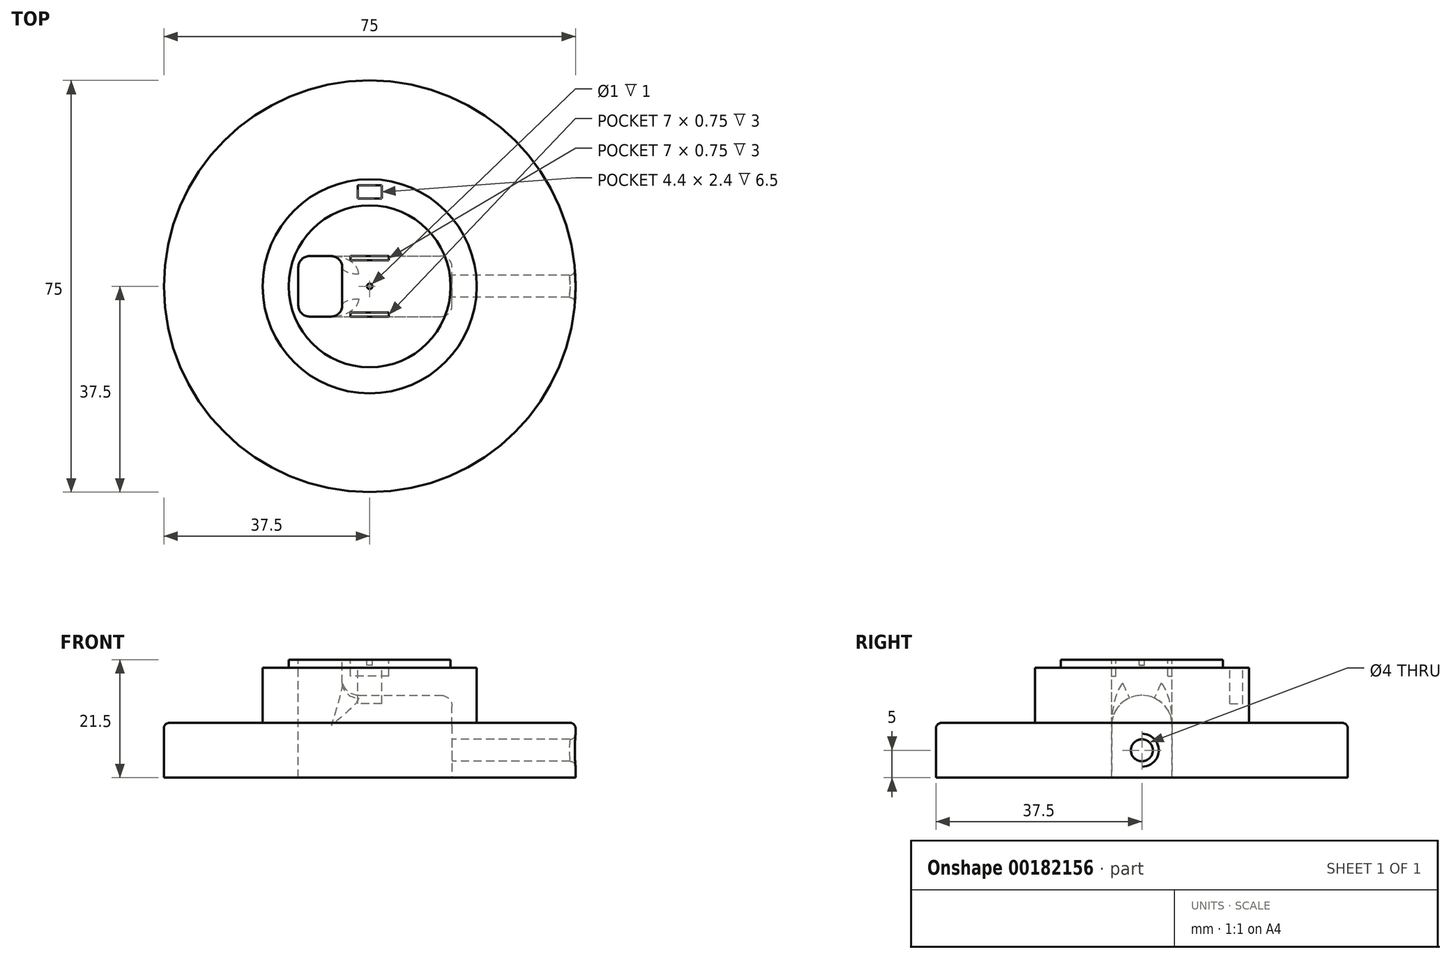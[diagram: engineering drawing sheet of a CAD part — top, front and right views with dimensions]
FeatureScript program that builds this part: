
annotation { "Feature Type Name" : "Feature", "Feature Type Description" : "" }
export const myFeature = defineFeature(function(context is Context, id is Id, definition is map)
    precondition{}
    {
        {
            var Q0;
            Q0=qCreatedBy(makeId("Top.planeOp"),FACE);
            var sketch = newSketch(context, id + "F0", { "sketchPlane" : qUnion([Q0])});
            skCircle(sketch, "E0", {"center": v(0, 0) * mm, "radius": 37.5 * mm});
            skSolve(sketch);
        }
        {
            var Q0;
            Q0 = qSketchRegion(id + "F0", true);
            extrude(context, id + "F1", {"entities" : qUnion([Q0]), "depth" : 10 * mm});
        }
        {
            var Q0;
            Q0=makeQuery(id+"F1.opExtrude","CAP_FACE",FACE,{"disambiguationData":[OSD([sQuery(id+"F0.wireOp",EDGE,"E0")])],"isStart":false});
            var sketch = newSketch(context, id + "F2", { "sketchPlane" : qUnion([Q0])});
            skCircle(sketch, "E1", {"center": v(0, 0) * mm, "radius": 19.5 * mm});
            skSolve(sketch);
        }
        {
            var Q0;
            Q0 = qSketchRegion(id + "F2", true);
            extrude(context, id + "F3", {"entities" : qUnion([Q0]), "operationType" : NewBodyOperationType.ADD, "depth" : 11.5 * mm});
        }
        {
            var Q0;
            Q0=makeQuery(id+"F3.opExtrude","CAP_FACE",FACE,{"disambiguationData":[OSD([sQuery(id+"F2.wireOp",EDGE,"E1")])],"isStart":false});
            var sketch = newSketch(context, id + "F4", { "sketchPlane" : qUnion([Q0])});
            skLineSegment(sketch, "E2.bottom", {"start": v(2.2, 16) * mm, "end": v(-2.2, 16) * mm});
            skLineSegment(sketch, "E2.top", {"start": v(2.2, 18.4) * mm, "end": v(-2.2, 18.4) * mm});
            skLineSegment(sketch, "E2.left", {"start": v(2.2, 16) * mm, "end": v(2.2, 18.4) * mm});
            skLineSegment(sketch, "E2.right", {"start": v(-2.2, 16) * mm, "end": v(-2.2, 18.4) * mm});
            skPoint(sketch, "E2.middle", {"position": v(0, 17.2) * mm});
            skCircle(sketch, "E3.0", {"center": v(0, 0) * mm, "radius": 19.5 * mm});
            skSolve(sketch);
        }
        {
            var Q0;
            Q0=makeQuery(id+"F4.imprint","IMPRINT",FACE,{"disambiguationData":[TD([[makeQuery(id+"F4.imprint","IMPRINT",EDGE,{"derivedFrom":sQuery(id+"F4.wireOp",EDGE,"E2.bottom")}),-1.0]])]});
            extrude(context, id + "F5", {"entities" : qUnion([Q0]), "operationType" : NewBodyOperationType.REMOVE, "oppositeDirection" : true, "depth" : 8 * mm});
        }
        {
            var Q0;
            Q0=makeQuery(id+"F3.opExtrude","CAP_FACE",FACE,{"disambiguationData":[OSD([sQuery(id+"F2.wireOp",EDGE,"E1")])],"isStart":false});
            var sketch = newSketch(context, id + "F6", { "sketchPlane" : qUnion([Q0])});
            skCircle(sketch, "E4", {"center": v(0, 0) * mm, "radius": 0.5 * mm});
            skSolve(sketch);
        }
        {
            var Q0;
            Q0 = qSketchRegion(id + "F6", true);
            extrude(context, id + "F7", {"entities" : qUnion([Q0]), "operationType" : NewBodyOperationType.REMOVE, "oppositeDirection" : true, "depth" : 1 * mm});
        }
        {
            var Q0;
            Q0=makeQuery(id+"F3.opExtrude","CAP_FACE",FACE,{"disambiguationData":[OSD([sQuery(id+"F2.wireOp",EDGE,"E1")])],"isStart":false});
            var sketch = newSketch(context, id + "F8", { "sketchPlane" : qUnion([Q0])});
            skLineSegment(sketch, "E5.bottom", {"start": v(6.92, -4.75) * mm, "end": v(-6.92, -4.75) * mm});
            skLineSegment(sketch, "E5.top", {"start": v(6.92, 4.75) * mm, "end": v(-6.92, 4.75) * mm});
            skLineSegment(sketch, "E5.left", {"start": v(6.92, -4.75) * mm, "end": v(6.92, 4.75) * mm});
            skLineSegment(sketch, "E5.right", {"start": v(-6.92, -4.75) * mm, "end": v(-6.92, 4.75) * mm});
            skPoint(sketch, "E5.middle", {"position": v(0, 0) * mm});
            skLineSegment(sketch, "E6.bottom", {"start": v(3.5, -5.5) * mm, "end": v(-3.5, -5.5) * mm});
            skLineSegment(sketch, "E6.top", {"start": v(3.5, 5.5) * mm, "end": v(-3.5, 5.5) * mm});
            skLineSegment(sketch, "E6.left", {"start": v(3.5, -5.5) * mm, "end": v(3.5, 5.5) * mm});
            skLineSegment(sketch, "E6.right", {"start": v(-3.5, -5.5) * mm, "end": v(-3.5, 5.5) * mm});
            skSolve(sketch);
        }
        {
            var Q0;
            {var subQ5=sQuery(id+"F8.wireOp",EDGE,"E6.top");Q0=makeQuery(id+"F8.imprint","IMPRINT",FACE,{"disambiguationData":[TD([[makeQuery(id+"F8.imprint","IMPRINT",EDGE,{"derivedFrom":subQ5}),1.0]])]});}
            var Q1;
            {var subQ5=sQuery(id+"F8.wireOp",EDGE,"E6.bottom");Q1=makeQuery(id+"F8.imprint","IMPRINT",FACE,{"disambiguationData":[TD([[makeQuery(id+"F8.imprint","IMPRINT",EDGE,{"derivedFrom":subQ5}),-1.0]])]});}
            extrude(context, id + "F9", {"entities" : qUnion([Q0, Q1]), "operationType" : NewBodyOperationType.REMOVE, "oppositeDirection" : true, "depth" : 3 * mm});
        }
        {
            var Q0;
            Q0=makeQuery(id+"F3.opExtrude","CAP_FACE",FACE,{"disambiguationData":[OSD([sQuery(id+"F2.wireOp",EDGE,"E1")])],"isStart":false});
            var sketch = newSketch(context, id + "F10", { "sketchPlane" : qUnion([Q0])});
            skLineSegment(sketch, "E7", {"start": v(0, 0) * mm, "end": v(-9, 0) * mm});
            skLineSegment(sketch, "E8.bottom", {"start": v(-13, 5.5) * mm, "end": v(-5, 5.5) * mm});
            skLineSegment(sketch, "E8.top", {"start": v(-13, -5.5) * mm, "end": v(-5, -5.5) * mm});
            skLineSegment(sketch, "E8.left", {"start": v(-13, 5.5) * mm, "end": v(-13, -5.5) * mm});
            skLineSegment(sketch, "E8.right", {"start": v(-5, 5.5) * mm, "end": v(-5, -5.5) * mm});
            skPoint(sketch, "E8.middle", {"position": v(-9, 0) * mm});
            skSolve(sketch);
        }
        {
            var Q0;
            Q0 = qSketchRegion(id + "F10", true);
            extrude(context, id + "F11", {"entities" : qUnion([Q0]), "operationType" : NewBodyOperationType.REMOVE, "oppositeDirection" : true, "depth" : 30 * mm});
        }
        {
            var Q0;
            Q0=makeQuery(id+"F1.opExtrude","CAP_FACE",FACE,{"disambiguationData":[OSD([sQuery(id+"F0.wireOp",EDGE,"E0")])],"isStart":true});
            var sketch = newSketch(context, id + "F12", { "sketchPlane" : qUnion([Q0])});
            skLineSegment(sketch, "E9.bottom", {"start": v(-5, 5.5) * mm, "end": v(15, 5.5) * mm});
            skLineSegment(sketch, "E9.top", {"start": v(-5, -5.5) * mm, "end": v(15, -5.5) * mm});
            skLineSegment(sketch, "E9.left", {"start": v(-5, 5.5) * mm, "end": v(-5, -5.5) * mm});
            skLineSegment(sketch, "E9.right", {"start": v(15, 5.5) * mm, "end": v(15, -5.5) * mm});
            skSolve(sketch);
        }
        {
            var Q0;
            Q0 = qSketchRegion(id + "F12", true);
            extrude(context, id + "F13", {"entities" : qUnion([Q0]), "operationType" : NewBodyOperationType.REMOVE, "oppositeDirection" : true, "depth" : 15 * mm});
        }
        {
            var Q0;
            Q0=makeQuery(id+"F13.boolean.opBoolean","COPY",FACE,{"derivedFrom":makeQuery(id+"F13.opExtrude","SWEPT_FACE",FACE,{"disambiguationData":[OSD([sQuery(id+"F12.wireOp",EDGE,"E9.right")])]})});
            var sketch = newSketch(context, id + "F14", { "sketchPlane" : qUnion([Q0])});
            skLineSegment(sketch, "E10", {"start": v(0, 0) * mm, "end": v(0, 5) * mm});
            skCircle(sketch, "E11", {"center": v(0, 5) * mm, "radius": 2 * mm});
            skSolve(sketch);
        }
        {
            var Q0;
            Q0 = qSketchRegion(id + "F14", true);
            extrude(context, id + "F15", {"entities" : qUnion([Q0]), "operationType" : NewBodyOperationType.REMOVE, "oppositeDirection" : true, "depth" : 40 * mm});
        }
        {
            var Q0;
            Q0=makeQuery(id+"F1.opExtrude","CAP_EDGE",EDGE,{"disambiguationData":[OSD([sQuery(id+"F0.wireOp",EDGE,"E0")])],"isStart":false});
            fillet(context, id + "F16", {"entities" : qUnion([Q0]), "radius" : 1 * mm, "tangentPropagation" : true, "allowEdgeOverflow" : false});
        }
        {
            var Q0;
            Q0=makeQuery(id+"F15.boolean.opBoolean","INTERSECT",EDGE,{"derivedFrom":[makeQuery(id+"F1.opExtrude","SWEPT_FACE",FACE,{"disambiguationData":[OSD([sQuery(id+"F0.wireOp",EDGE,"E0")])]}),makeQuery(id+"F15.opExtrude","SWEPT_FACE",FACE,{"disambiguationData":[OSD([sQuery(id+"F14.wireOp",EDGE,"E11")])]})]});
            fillet(context, id + "F17", {"entities" : qUnion([Q0]), "radius" : 1 * mm, "tangentPropagation" : true, "allowEdgeOverflow" : false});
        }
        {
            var Q0;
            Q0=makeQuery(id+"F13.boolean.opBoolean","COPY",EDGE,{"derivedFrom":makeQuery(id+"F13.opExtrude","CAP_EDGE",EDGE,{"disambiguationData":[OSD([sQuery(id+"F12.wireOp",EDGE,"E9.bottom")])],"isStart":false})});
            var Q1;
            Q1=makeQuery(id+"F13.boolean.opBoolean","COPY",EDGE,{"derivedFrom":makeQuery(id+"F13.opExtrude","CAP_EDGE",EDGE,{"disambiguationData":[OSD([sQuery(id+"F12.wireOp",EDGE,"E9.top")])],"isStart":false})});
            fillet(context, id + "F18", {"entities" : qUnion([Q0, Q1]), "radius" : 5.5 * mm, "tangentPropagation" : true, "allowEdgeOverflow" : false});
        }
        {
            var Q0;
            Q0=makeQuery(id+"F11.boolean.opBoolean","COPY",EDGE,{"derivedFrom":makeQuery(id+"F11.opExtrude","SWEPT_EDGE",EDGE,{"disambiguationData":[OSD([sQuery(id+"F10.wireOp",EDGE,"E8.bottom"),sQuery(id+"F10.wireOp",EDGE,"E8.left")])]})});
            var Q1;
            Q1=makeQuery(id+"F11.boolean.opBoolean","COPY",EDGE,{"derivedFrom":makeQuery(id+"F11.opExtrude","SWEPT_EDGE",EDGE,{"disambiguationData":[OSD([sQuery(id+"F10.wireOp",EDGE,"E8.bottom"),sQuery(id+"F10.wireOp",EDGE,"E8.right")])]})});
            var Q2;
            Q2=makeQuery(id+"F11.boolean.opBoolean","COPY",EDGE,{"derivedFrom":makeQuery(id+"F11.opExtrude","SWEPT_EDGE",EDGE,{"disambiguationData":[OSD([sQuery(id+"F10.wireOp",EDGE,"E8.top"),sQuery(id+"F10.wireOp",EDGE,"E8.right")])]})});
            var Q3;
            Q3=makeQuery(id+"F11.boolean.opBoolean","COPY",EDGE,{"derivedFrom":makeQuery(id+"F11.opExtrude","SWEPT_EDGE",EDGE,{"disambiguationData":[OSD([sQuery(id+"F10.wireOp",EDGE,"E8.top"),sQuery(id+"F10.wireOp",EDGE,"E8.left")])]})});
            var Q4;
            Q4=makeQuery(id+"F13.boolean.opBoolean","COPY",EDGE,{"derivedFrom":makeQuery(id+"F13.opExtrude","SWEPT_EDGE",EDGE,{"disambiguationData":[OSD([sQuery(id+"F12.wireOp",EDGE,"E9.top"),sQuery(id+"F12.wireOp",EDGE,"E9.right")])]})});
            fillet(context, id + "F19", {"entities" : qUnion([Q0, Q1, Q2, Q3, Q4]), "radius" : 2 * mm, "tangentPropagation" : true, "allowEdgeOverflow" : false});
        }
        {
            var Q0;
            Q0=makeQuery(id+"F19.opFillet","BLEND_EDGE",EDGE,{"blendedFrom":[makeQuery(id+"F11.boolean.opBoolean","COPY",EDGE,{"derivedFrom":makeQuery(id+"F11.opExtrude","SWEPT_EDGE",EDGE,{"disambiguationData":[OSD([sQuery(id+"F10.wireOp",EDGE,"E8.bottom"),sQuery(id+"F10.wireOp",EDGE,"E8.right")])]})}),makeQuery(id+"F18.opFillet","BLEND_FACE",FACE,{"disambiguationData":[OSD([sQuery(id+"F12.wireOp",EDGE,"E9.bottom")])]})],"blendedInto":[makeQuery(id+"F18.opFillet","BLEND_FACE",FACE,{"disambiguationData":[OSD([sQuery(id+"F12.wireOp",EDGE,"E9.bottom")])]})]});
            fillet(context, id + "F20", {"entities" : qUnion([Q0]), "radius" : 3 * mm, "tangentPropagation" : true, "allowEdgeOverflow" : false});
        }
        {
            var Q0;
            Q0=makeQuery(id+"F3.opExtrude","CAP_FACE",FACE,{"disambiguationData":[OSD([sQuery(id+"F2.wireOp",EDGE,"E1")])],"isStart":false});
            var sketch = newSketch(context, id + "F21", { "sketchPlane" : qUnion([Q0])});
            skCircle(sketch, "E12", {"center": v(0, 0) * mm, "radius": 14.75 * mm});
            skCircle(sketch, "E13", {"center": v(0, 0) * mm, "radius": 23.62 * mm});
            skSolve(sketch);
        }
        {
            var Q0;
            Q0 = qSketchRegion(id + "F21", true);
            extrude(context, id + "F22", {"entities" : qUnion([Q0]), "operationType" : NewBodyOperationType.REMOVE, "oppositeDirection" : true, "depth" : 1.5 * mm});
        }
    });
